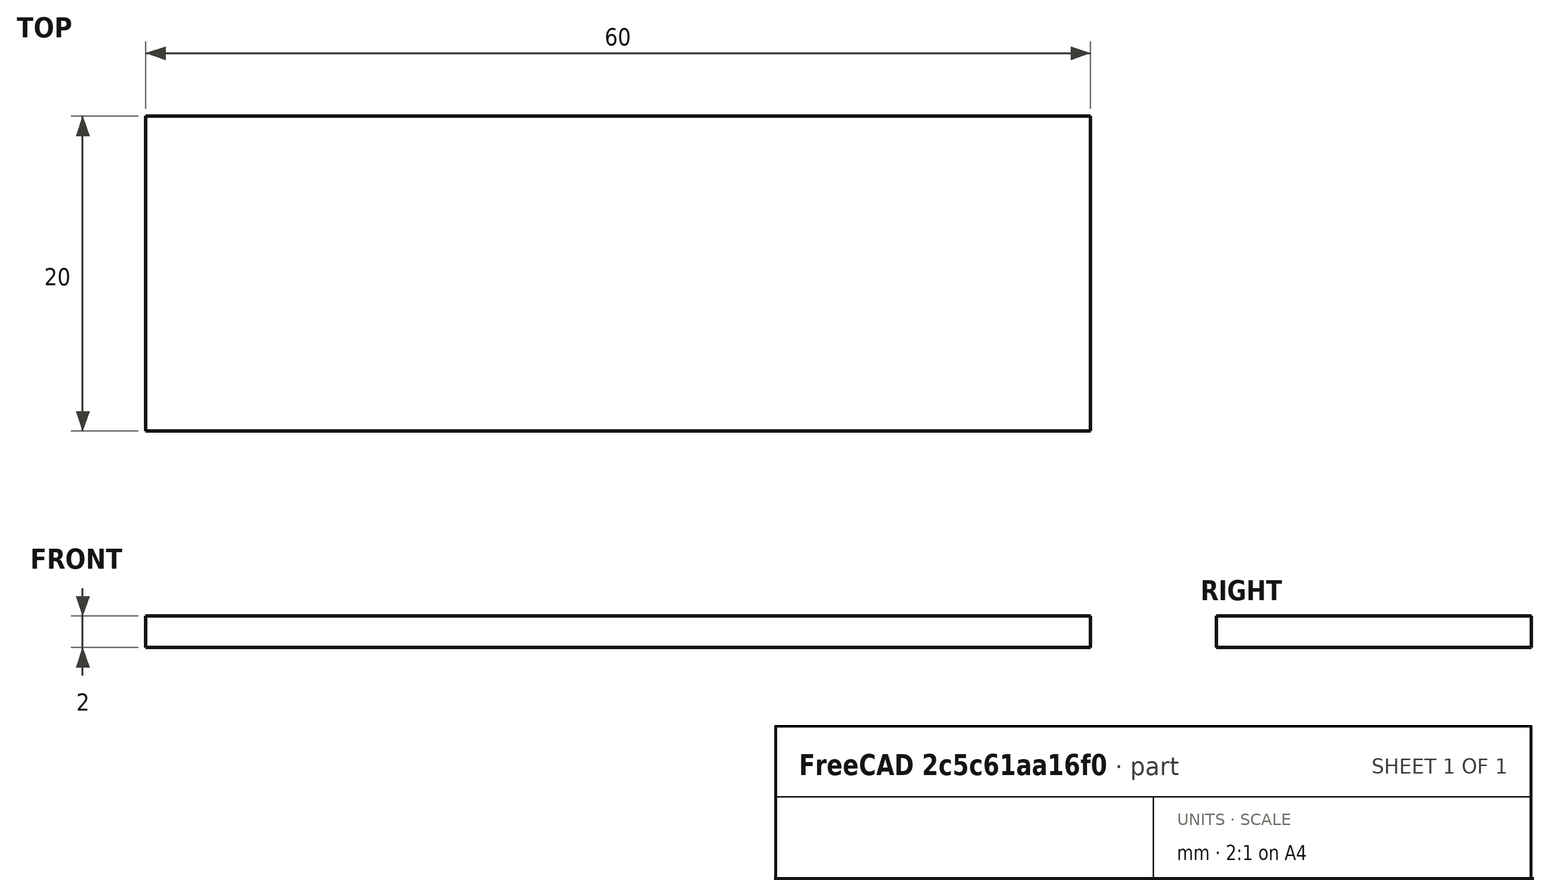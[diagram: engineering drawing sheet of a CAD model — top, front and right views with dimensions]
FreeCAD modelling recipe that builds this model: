
FCSTD DOCUMENT  (FreeCAD 0.19R24291 (Git))
Label: base_sensorultrasonidos
License: All rights reserved
LicenseURL: http://en.wikipedia.org/wiki/All_rights_reserved
objects: Sketcher::SketchObject×1, PartDesign::Pad×1, PartDesign::Body×1
note: 4 computed .brp shape members not serialized (recipe doc carries the construction recipe); baked Part::Feature solids carry a one-line shape summary decoded from their .brp

FEATURE [Sketcher::SketchObject] Sketch
  FullyConstrained = false
  MapMode = 5
  Support = -> [XY_Plane]
  sketch-geometry (4):
    g0: LineSegment StartX=-25.0233 StartY=13.931 StartZ=0 EndX=34.9767 EndY=13.931 EndZ=0
    g1: LineSegment StartX=34.9767 StartY=13.931 StartZ=0 EndX=34.9767 EndY=-6.06904 EndZ=0
    g2: LineSegment StartX=34.9767 StartY=-6.06904 StartZ=0 EndX=-25.0233 EndY=-6.06904 EndZ=0
    g3: LineSegment StartX=-25.0233 StartY=-6.06904 StartZ=0 EndX=-25.0233 EndY=13.931 EndZ=0
  constraints (10):
    c: Coincident(g0,g1)
    c: Coincident(g1,g2)
    c: Coincident(g2,g3)
    c: Coincident(g3,g0)
    c: Horizontal(g0)
    c: Horizontal(g2)
    c: Vertical(g1)
    c: Vertical(g3)
    c: DistanceX(g0,g0) = 60
    c: DistanceY(g1,g1) = 20
FEATURE [PartDesign::Pad] Pad
  Direction = (1,1,1)
  Length = 2
  Length2 = 100
  Profile = -> Sketch
  Type = 0
FEATURE [PartDesign::Body] Body  label="base_ultra"
  Group = -> [Sketch,Pad]
  Origin = -> Origin
  Tip = -> Pad
